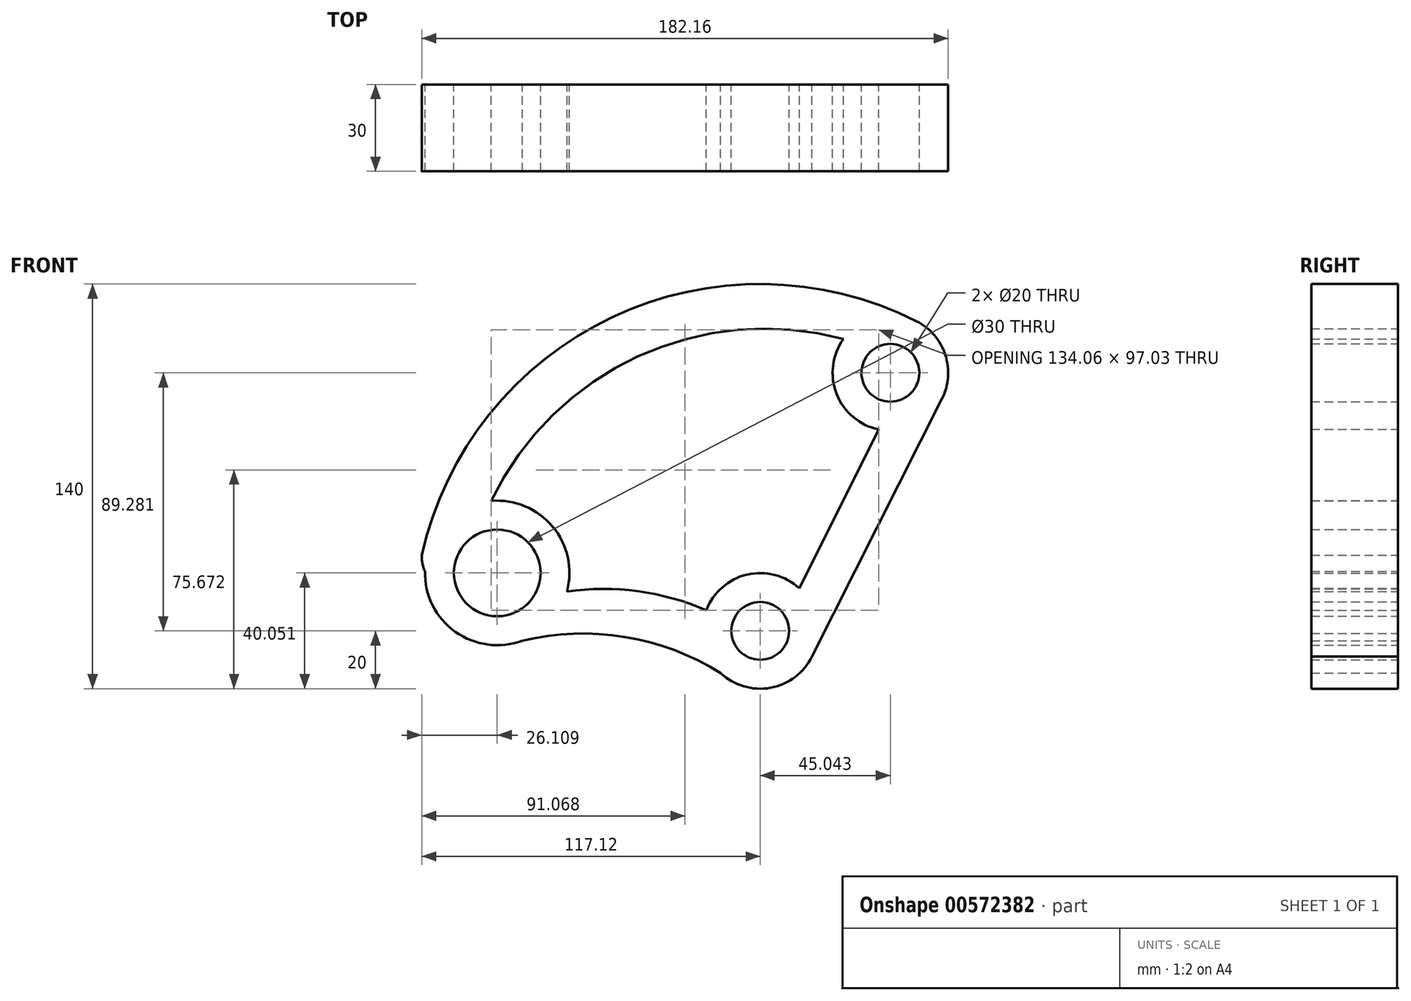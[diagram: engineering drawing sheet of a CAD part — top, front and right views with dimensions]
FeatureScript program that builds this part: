
annotation { "Feature Type Name" : "Feature", "Feature Type Description" : "" }
export const myFeature = defineFeature(function(context is Context, id is Id, definition is map)
    precondition{}
    {
        {
            var Q0;
            Q0=qCreatedBy(makeId("Front.planeOp"),FACE);
            var sketch = newSketch(context, id + "F0", { "sketchPlane" : qUnion([Q0])});
            skArc(sketch, "E0", {"start": v(54.05, 107.14) * mm, "mid": v(-51.3, 108.48) * mm, "end": v(-117.1, 26.21) * mm});
            skCircle(sketch, "E1", {"center": v(0, 0) * mm, "radius": 10 * mm});
            skArc(sketch, "E2", {"start": v(13.53, 14.73) * mm, "mid": v(-19.66, -3.69) * mm, "end": v(17.95, -8.82) * mm});
            skArc(sketch, "E3", {"start": v(62.9, 80.27) * mm, "mid": v(36.35, 107.3) * mm, "end": v(40.98, 69.7) * mm});
            skLineSegment(sketch, "E4", {"start": v(17.76, -9.2) * mm, "end": v(62.9, 80.27) * mm});
            skLineSegment(sketch, "E5", {"start": v(13.53, 14.73) * mm, "end": v(40.98, 69.7) * mm});
            skCircle(sketch, "E6", {"center": v(45.04, 89.28) * mm, "radius": 10 * mm});
            skCircle(sketch, "E7", {"center": v(-91.01, 20.05) * mm, "radius": 25 * mm});
            skCircle(sketch, "E8", {"center": v(-91.01, 20.05) * mm, "radius": 15 * mm});
            skArc(sketch, "E9.trimOffspring", {"start": v(28.81, 100.97) * mm, "mid": v(-42.24, 94.97) * mm, "end": v(-93.08, 44.97) * mm});
            skPoint(sketch, "E10", {"position": v(-117.1, 26.21) * mm});
            skPoint(sketch, "E11", {"position": v(54.05, 107.14) * mm});
            skArc(sketch, "E12", {"start": v(-13.72, -14.56) * mm, "mid": v(-49.2, -1.74) * mm, "end": v(-86.8, -4.6) * mm});
            skArc(sketch, "E13", {"start": v(-18.68, 7.16) * mm, "mid": v(-42.32, 13.71) * mm, "end": v(-66.85, 13.64) * mm});
            skArc(sketch, "E14", {"start": v(-117.1, 26.21) * mm, "mid": v(-116.9, 23.34) * mm, "end": v(-116, 20.6) * mm});
            skSolve(sketch);
        }
        {
            var Q0;
            Q0 = qSketchRegion(id + "F0", true);
            extrude(context, id + "F1", {"entities" : qUnion([Q0]), "depth" : 30 * mm, "offsetDistance" : 25 * mm});
        }
    });
